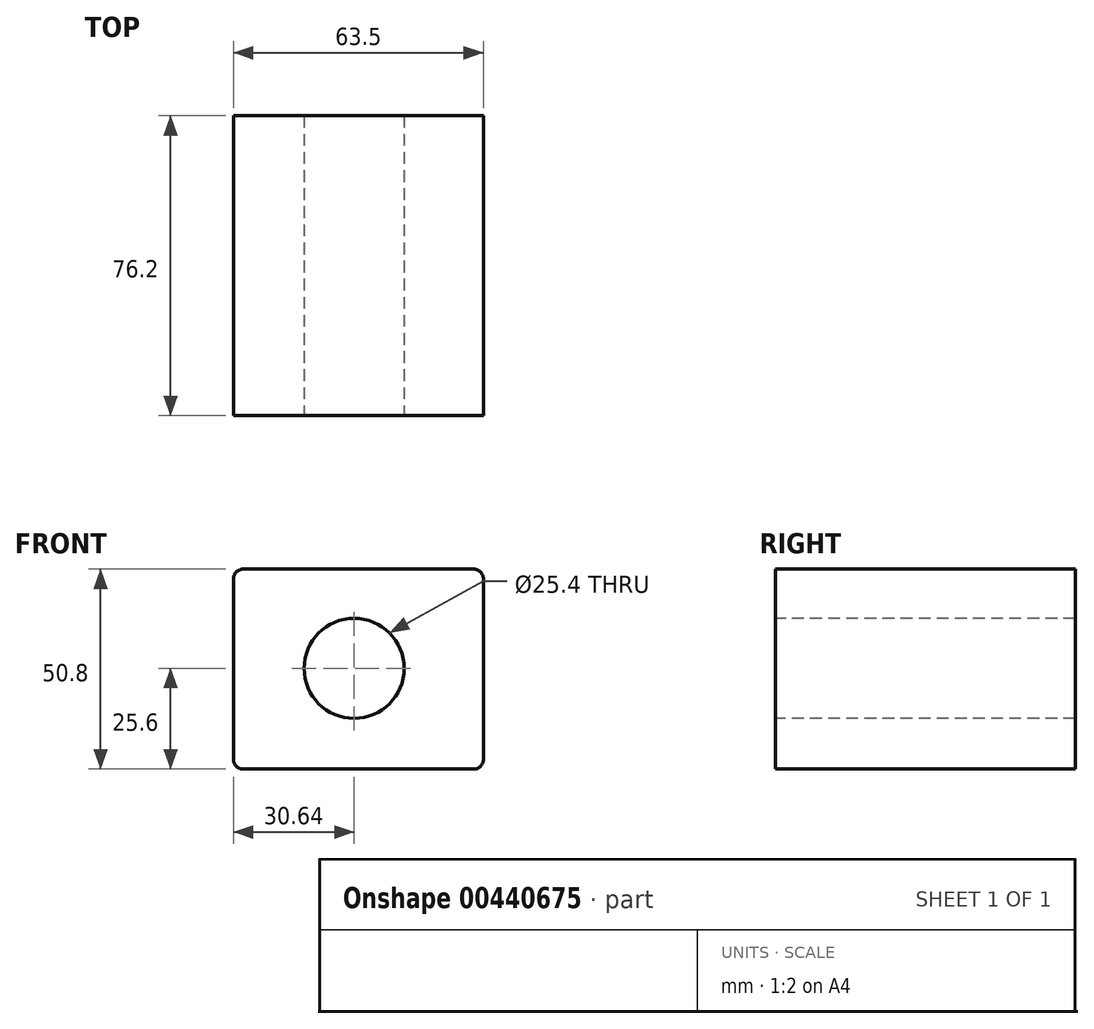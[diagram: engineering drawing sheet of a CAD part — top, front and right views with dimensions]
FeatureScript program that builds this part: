
annotation { "Feature Type Name" : "Feature", "Feature Type Description" : "" }
export const myFeature = defineFeature(function(context is Context, id is Id, definition is map)
    precondition{}
    {
        {
            var Q0;
            Q0=qCreatedBy(makeId("Front.planeOp"),FACE);
            var sketch = newSketch(context, id + "F0", { "sketchPlane" : qUnion([Q0])});
            skLineSegment(sketch, "E0.bottom", {"start": v(-30.64, 25.2) * mm, "end": v(32.86, 25.2) * mm});
            skLineSegment(sketch, "E0.top", {"start": v(-30.64, -25.6) * mm, "end": v(32.86, -25.6) * mm});
            skLineSegment(sketch, "E0.left", {"start": v(-30.64, 25.2) * mm, "end": v(-30.64, -25.6) * mm});
            skLineSegment(sketch, "E0.right", {"start": v(32.86, 25.2) * mm, "end": v(32.86, -25.6) * mm});
            skSolve(sketch);
        }
        {
            var Q0;
            Q0=makeQuery(id+"F0.imprint","IMPRINT",FACE,{"disambiguationData":[TD([[makeQuery(id+"F0.imprint","IMPRINT",EDGE,{"derivedFrom":sQuery(id+"F0.wireOp",EDGE,"E0.bottom")}),-1.0]])]});
            extrude(context, id + "F1", {"entities" : qUnion([Q0]), "flatOperationType" : FlatOperationType.REMOVE, "offsetDistance" : 25.4 * mm, "depth" : 76.2 * mm, "domain" : OperationDomain.MODEL});
        }
        {
            var Q0;
            Q0=makeQuery(id+"F1.opExtrude","SWEPT_EDGE",EDGE,{"disambiguationData":[OSD([sQuery(id+"F0.wireOp",EDGE,"E0.bottom"),sQuery(id+"F0.wireOp",EDGE,"E0.right")])]});
            var Q1;
            Q1=makeQuery(id+"F1.opExtrude","SWEPT_EDGE",EDGE,{"disambiguationData":[OSD([sQuery(id+"F0.wireOp",EDGE,"E0.bottom"),sQuery(id+"F0.wireOp",EDGE,"E0.left")])]});
            var Q2;
            Q2=makeQuery(id+"F1.opExtrude","SWEPT_EDGE",EDGE,{"disambiguationData":[OSD([sQuery(id+"F0.wireOp",EDGE,"E0.top"),sQuery(id+"F0.wireOp",EDGE,"E0.right")])]});
            var Q3;
            Q3=makeQuery(id+"F1.opExtrude","SWEPT_EDGE",EDGE,{"disambiguationData":[OSD([sQuery(id+"F0.wireOp",EDGE,"E0.top"),sQuery(id+"F0.wireOp",EDGE,"E0.left")])]});
            fillet(context, id + "F2", {"entities" : qUnion([Q0, Q1, Q2, Q3]), "radius" : 2.45 * mm, "tangentPropagation" : true, "allowEdgeOverflow" : false});
        }
        {
            var Q0;
            Q0=makeQuery(id+"F1.opExtrude","CAP_FACE",FACE,{"disambiguationData":[OSD([sQuery(id+"F0.wireOp",EDGE,"E0.bottom"),sQuery(id+"F0.wireOp",EDGE,"E0.top"),sQuery(id+"F0.wireOp",EDGE,"E0.left"),sQuery(id+"F0.wireOp",EDGE,"E0.right")])],"isStart":false});
            var sketch = newSketch(context, id + "F3", { "sketchPlane" : qUnion([Q0])});
            skCircle(sketch, "E1", {"center": v(0, 0) * mm, "radius": 12.7 * mm});
            skSolve(sketch);
        }
        {
            var Q0;
            Q0=makeQuery(id+"F3.imprint","IMPRINT",FACE,{"disambiguationData":[TD([[makeQuery(id+"F3.imprint","IMPRINT",EDGE,{"derivedFrom":sQuery(id+"F3.wireOp",EDGE,"E1")}),1.0]])]});
            var Q1;
            Q1=makeQuery(id+"F1.opExtrude","CAP_FACE",FACE,{"disambiguationData":[OSD([sQuery(id+"F0.wireOp",EDGE,"E0.bottom"),sQuery(id+"F0.wireOp",EDGE,"E0.top"),sQuery(id+"F0.wireOp",EDGE,"E0.left"),sQuery(id+"F0.wireOp",EDGE,"E0.right")])],"isStart":true});
            extrude(context, id + "F4", {"entities" : qUnion([Q0]), "operationType" : NewBodyOperationType.REMOVE, "endBound" : BoundingType.UP_TO_SURFACE, "oppositeDirection" : true, "endBoundEntityFace" : qUnion([Q1]), "depth" : 25.4 * mm});
        }
    });
